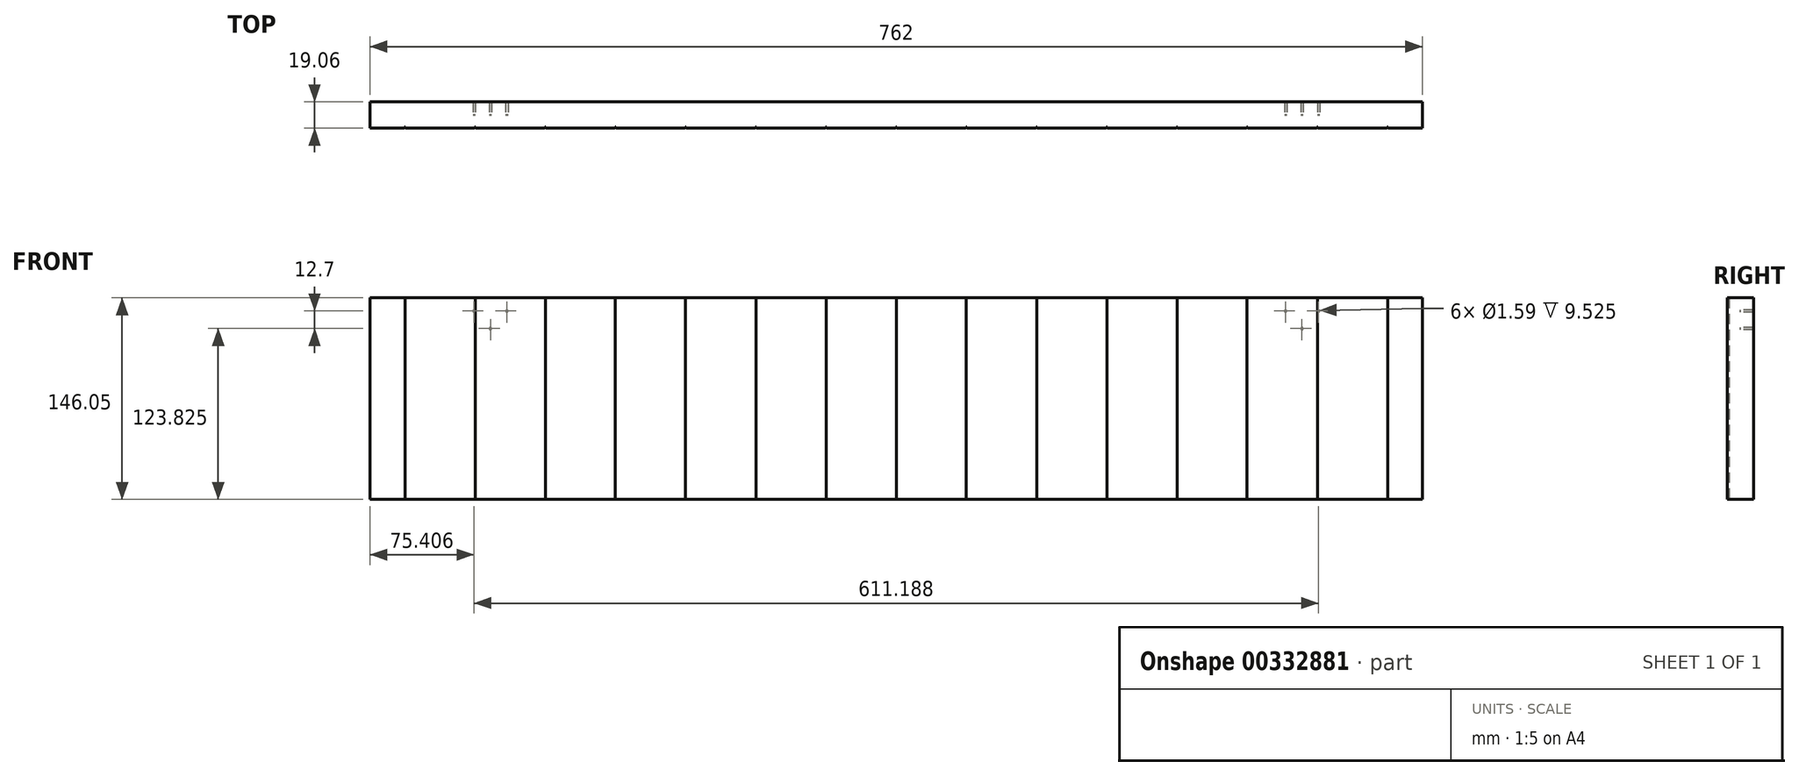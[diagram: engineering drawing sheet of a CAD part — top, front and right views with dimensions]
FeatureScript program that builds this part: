
annotation { "Feature Type Name" : "Feature", "Feature Type Description" : "" }
export const myFeature = defineFeature(function(context is Context, id is Id, definition is map)
    precondition{}
    {
        {
            var Q0;
            Q0=qCreatedBy(makeId("Top.planeOp"),FACE);
            var sketch = newSketch(context, id + "F0", { "sketchPlane" : qUnion([Q0])});
            skLineSegment(sketch, "E0.bottom", {"start": v(508, -9.53) * mm, "end": v(458.22, -9.53) * mm});
            skLineSegment(sketch, "E0.top", {"start": v(508, 9.53) * mm, "end": v(-508, 9.53) * mm});
            skLineSegment(sketch, "E0.left", {"start": v(508, 9.53) * mm, "end": v(508, -9.53) * mm});
            skLineSegment(sketch, "E0.right", {"start": v(-508, 9.53) * mm, "end": v(-508, -9.53) * mm});
            skPoint(sketch, "E0.middle", {"position": v(0, 0) * mm});
            skArc(sketch, "E1", {"start": v(-509.02, -9.53) * mm, "mid": v(-508.3, -9.23) * mm, "end": v(-508, -8.5) * mm});
            skArc(sketch, "E2", {"start": v(-508, -8.5) * mm, "mid": v(-507.7, -9.23) * mm, "end": v(-506.98, -9.52) * mm});
            skArc(sketch, "E3.1.0.0", {"start": v(-458.22, -9.53) * mm, "mid": v(-457.5, -9.23) * mm, "end": v(-457.2, -8.5) * mm});
            skArc(sketch, "E3.1.0.1", {"start": v(-457.2, -8.5) * mm, "mid": v(-456.9, -9.23) * mm, "end": v(-456.18, -9.52) * mm});
            skArc(sketch, "E3.2.0.0", {"start": v(-407.42, -9.53) * mm, "mid": v(-406.7, -9.23) * mm, "end": v(-406.4, -8.5) * mm});
            skArc(sketch, "E3.2.0.1", {"start": v(-406.4, -8.5) * mm, "mid": v(-406.1, -9.23) * mm, "end": v(-405.38, -9.52) * mm});
            skArc(sketch, "E3.3.0.0", {"start": v(-356.62, -9.53) * mm, "mid": v(-355.9, -9.23) * mm, "end": v(-355.6, -8.5) * mm});
            skArc(sketch, "E3.3.0.1", {"start": v(-355.6, -8.5) * mm, "mid": v(-355.3, -9.23) * mm, "end": v(-354.58, -9.52) * mm});
            skArc(sketch, "E3.4.0.0", {"start": v(-305.82, -9.53) * mm, "mid": v(-305.1, -9.23) * mm, "end": v(-304.8, -8.5) * mm});
            skArc(sketch, "E3.4.0.1", {"start": v(-304.8, -8.5) * mm, "mid": v(-304.5, -9.23) * mm, "end": v(-303.78, -9.52) * mm});
            skArc(sketch, "E3.5.0.0", {"start": v(-255.02, -9.53) * mm, "mid": v(-254.3, -9.23) * mm, "end": v(-254, -8.5) * mm});
            skArc(sketch, "E3.5.0.1", {"start": v(-254, -8.5) * mm, "mid": v(-253.7, -9.23) * mm, "end": v(-252.98, -9.52) * mm});
            skArc(sketch, "E3.6.0.0", {"start": v(-204.22, -9.53) * mm, "mid": v(-203.5, -9.23) * mm, "end": v(-203.2, -8.5) * mm});
            skArc(sketch, "E3.6.0.1", {"start": v(-203.2, -8.5) * mm, "mid": v(-202.9, -9.23) * mm, "end": v(-202.18, -9.52) * mm});
            skArc(sketch, "E3.7.0.0", {"start": v(-153.42, -9.53) * mm, "mid": v(-152.7, -9.23) * mm, "end": v(-152.4, -8.5) * mm});
            skArc(sketch, "E3.7.0.1", {"start": v(-152.4, -8.5) * mm, "mid": v(-152.1, -9.23) * mm, "end": v(-151.38, -9.52) * mm});
            skArc(sketch, "E3.8.0.0", {"start": v(-102.62, -9.53) * mm, "mid": v(-101.9, -9.23) * mm, "end": v(-101.6, -8.5) * mm});
            skArc(sketch, "E3.8.0.1", {"start": v(-101.6, -8.5) * mm, "mid": v(-101.3, -9.23) * mm, "end": v(-100.58, -9.52) * mm});
            skArc(sketch, "E3.9.0.0", {"start": v(-51.82, -9.53) * mm, "mid": v(-51.1, -9.23) * mm, "end": v(-50.8, -8.5) * mm});
            skArc(sketch, "E3.9.0.1", {"start": v(-50.8, -8.5) * mm, "mid": v(-50.5, -9.23) * mm, "end": v(-49.78, -9.52) * mm});
            skArc(sketch, "E3.10.0.0", {"start": v(-1.02, -9.53) * mm, "mid": v(-0.3, -9.23) * mm, "end": v(0, -8.5) * mm});
            skArc(sketch, "E3.10.0.1", {"start": v(0, -8.5) * mm, "mid": v(0.3, -9.23) * mm, "end": v(1.02, -9.52) * mm});
            skArc(sketch, "E3.11.0.0", {"start": v(49.78, -9.53) * mm, "mid": v(50.5, -9.23) * mm, "end": v(50.8, -8.5) * mm});
            skArc(sketch, "E3.11.0.1", {"start": v(50.8, -8.5) * mm, "mid": v(51.1, -9.23) * mm, "end": v(51.82, -9.52) * mm});
            skArc(sketch, "E3.12.0.0", {"start": v(100.58, -9.53) * mm, "mid": v(101.3, -9.23) * mm, "end": v(101.6, -8.5) * mm});
            skArc(sketch, "E3.12.0.1", {"start": v(101.6, -8.5) * mm, "mid": v(101.9, -9.23) * mm, "end": v(102.62, -9.52) * mm});
            skArc(sketch, "E3.13.0.0", {"start": v(151.38, -9.53) * mm, "mid": v(152.1, -9.23) * mm, "end": v(152.4, -8.5) * mm});
            skArc(sketch, "E3.13.0.1", {"start": v(152.4, -8.5) * mm, "mid": v(152.7, -9.23) * mm, "end": v(153.42, -9.52) * mm});
            skArc(sketch, "E3.14.0.0", {"start": v(202.18, -9.53) * mm, "mid": v(202.9, -9.23) * mm, "end": v(203.2, -8.5) * mm});
            skArc(sketch, "E3.14.0.1", {"start": v(203.2, -8.5) * mm, "mid": v(203.5, -9.23) * mm, "end": v(204.22, -9.52) * mm});
            skArc(sketch, "E3.15.0.0", {"start": v(252.98, -9.53) * mm, "mid": v(253.7, -9.23) * mm, "end": v(254, -8.5) * mm});
            skArc(sketch, "E3.15.0.1", {"start": v(254, -8.5) * mm, "mid": v(254.3, -9.23) * mm, "end": v(255.02, -9.52) * mm});
            skArc(sketch, "E3.16.0.0", {"start": v(303.78, -9.53) * mm, "mid": v(304.5, -9.23) * mm, "end": v(304.8, -8.5) * mm});
            skArc(sketch, "E3.16.0.1", {"start": v(304.8, -8.5) * mm, "mid": v(305.1, -9.23) * mm, "end": v(305.82, -9.52) * mm});
            skArc(sketch, "E3.17.0.0", {"start": v(354.58, -9.53) * mm, "mid": v(355.3, -9.23) * mm, "end": v(355.6, -8.5) * mm});
            skArc(sketch, "E3.17.0.1", {"start": v(355.6, -8.5) * mm, "mid": v(355.9, -9.23) * mm, "end": v(356.62, -9.52) * mm});
            skArc(sketch, "E3.18.0.0", {"start": v(405.38, -9.53) * mm, "mid": v(406.1, -9.23) * mm, "end": v(406.4, -8.5) * mm});
            skArc(sketch, "E3.18.0.1", {"start": v(406.4, -8.5) * mm, "mid": v(406.7, -9.23) * mm, "end": v(407.42, -9.52) * mm});
            skArc(sketch, "E3.19.0.0", {"start": v(456.18, -9.53) * mm, "mid": v(456.9, -9.23) * mm, "end": v(457.2, -8.5) * mm});
            skArc(sketch, "E3.19.0.1", {"start": v(457.2, -8.5) * mm, "mid": v(457.5, -9.23) * mm, "end": v(458.22, -9.52) * mm});
            skLineSegment(sketch, "E3.direction1", {"start": v(-506.98, -9.53) * mm, "end": v(-458.22, -9.53) * mm, "construction": true});
            skLineSegment(sketch, "E4.trimOffspring", {"start": v(-458.22, -9.53) * mm, "end": v(-508, -9.53) * mm});
            skLineSegment(sketch, "E5.trimOffspring", {"start": v(-407.42, -9.53) * mm, "end": v(-456.18, -9.53) * mm});
            skLineSegment(sketch, "E6.trimOffspring", {"start": v(-356.62, -9.53) * mm, "end": v(-405.38, -9.53) * mm});
            skLineSegment(sketch, "E7.trimOffspring", {"start": v(-305.82, -9.53) * mm, "end": v(-354.58, -9.53) * mm});
            skLineSegment(sketch, "E8.trimOffspring", {"start": v(-255.02, -9.53) * mm, "end": v(-303.78, -9.53) * mm});
            skLineSegment(sketch, "E9.trimOffspring", {"start": v(-204.22, -9.53) * mm, "end": v(-252.98, -9.53) * mm});
            skLineSegment(sketch, "E10.trimOffspring", {"start": v(-153.42, -9.53) * mm, "end": v(-202.18, -9.53) * mm});
            skLineSegment(sketch, "E11.trimOffspring", {"start": v(-102.62, -9.53) * mm, "end": v(-151.38, -9.53) * mm});
            skLineSegment(sketch, "E12.trimOffspring", {"start": v(-51.82, -9.53) * mm, "end": v(-100.58, -9.53) * mm});
            skLineSegment(sketch, "E13.trimOffspring", {"start": v(-1.02, -9.53) * mm, "end": v(-49.78, -9.53) * mm});
            skLineSegment(sketch, "E14.trimOffspring", {"start": v(49.78, -9.53) * mm, "end": v(1.02, -9.53) * mm});
            skLineSegment(sketch, "E15.trimOffspring", {"start": v(100.58, -9.53) * mm, "end": v(51.82, -9.53) * mm});
            skLineSegment(sketch, "E16.trimOffspring", {"start": v(151.38, -9.53) * mm, "end": v(102.62, -9.53) * mm});
            skLineSegment(sketch, "E17.trimOffspring", {"start": v(202.18, -9.53) * mm, "end": v(153.42, -9.53) * mm});
            skLineSegment(sketch, "E18.trimOffspring", {"start": v(252.98, -9.53) * mm, "end": v(204.22, -9.53) * mm});
            skLineSegment(sketch, "E19.trimOffspring", {"start": v(303.78, -9.53) * mm, "end": v(255.02, -9.53) * mm});
            skLineSegment(sketch, "E20.trimOffspring", {"start": v(354.58, -9.53) * mm, "end": v(305.82, -9.53) * mm});
            skLineSegment(sketch, "E21.trimOffspring", {"start": v(405.38, -9.53) * mm, "end": v(356.62, -9.53) * mm});
            skLineSegment(sketch, "E22.trimOffspring", {"start": v(456.18, -9.53) * mm, "end": v(407.42, -9.53) * mm});
            skSolve(sketch);
        }
        {
            var Q0;
            Q0=qSketchRegion(id+"F0",true);
            extrude(context, id + "F1", {"entities" : qUnion([Q0]), "depth" : 146.05 * mm});
        }
        {
            var Q0;
            Q0=qCreatedBy(makeId("Top.planeOp"),FACE);
            var sketch = newSketch(context, id + "F2", { "sketchPlane" : qUnion([Q0])});
            skLineSegment(sketch, "E23.bottom", {"start": v(381, -89.59) * mm, "end": v(724.07, -89.59) * mm});
            skLineSegment(sketch, "E23.top", {"start": v(381, 47.64) * mm, "end": v(724.07, 47.64) * mm});
            skLineSegment(sketch, "E23.left", {"start": v(381, -89.59) * mm, "end": v(381, 47.64) * mm});
            skLineSegment(sketch, "E23.right", {"start": v(724.07, -89.59) * mm, "end": v(724.07, 47.64) * mm});
            skLineSegment(sketch, "E24.bottom", {"start": v(-381, -137.09) * mm, "end": v(-685.36, -137.09) * mm});
            skLineSegment(sketch, "E24.top", {"start": v(-381, 58.2) * mm, "end": v(-685.36, 58.2) * mm});
            skLineSegment(sketch, "E24.left", {"start": v(-381, -137.09) * mm, "end": v(-381, 58.2) * mm});
            skLineSegment(sketch, "E24.right", {"start": v(-685.36, -137.09) * mm, "end": v(-685.36, 58.2) * mm});
            skSolve(sketch);
        }
        {
            var Q0;
            Q0=qSketchRegion(id+"F2",true);
            extrude(context, id + "F3", {"entities" : qUnion([Q0]), "operationType" : NewBodyOperationType.REMOVE, "depth" : 1143 * mm});
        }
        {
            var Q0;
            Q0=qCreatedBy(makeId("Front.planeOp"),FACE);
            var sketch = newSketch(context, id + "F4", { "sketchPlane" : qUnion([Q0])});
            skLineSegment(sketch, "E25", {"start": v(381, 136.53) * mm, "end": v(-381, 136.52) * mm, "construction": true});
            skLineSegment(sketch, "E26.bottom", {"start": v(381, 193.1) * mm, "end": v(-381, 193.1) * mm, "construction": true});
            skLineSegment(sketch, "E26.top", {"start": v(381, 79.95) * mm, "end": v(-381, 79.95) * mm, "construction": true});
            skLineSegment(sketch, "E26.left", {"start": v(381, 193.1) * mm, "end": v(381, 79.95) * mm, "construction": true});
            skLineSegment(sketch, "E26.right", {"start": v(-381, 193.1) * mm, "end": v(-381, 79.95) * mm, "construction": true});
            skPoint(sketch, "E26.middle", {"position": v(0, 136.53) * mm});
            skLineSegment(sketch, "E27", {"start": v(-293.69, 193.1) * mm, "end": v(-293.69, 79.95) * mm, "construction": true});
            skLineSegment(sketch, "E28", {"start": v(-293.69, 123.82) * mm, "end": v(293.69, 123.83) * mm, "construction": true});
            skLineSegment(sketch, "E29", {"start": v(293.69, 193.1) * mm, "end": v(293.69, 79.95) * mm, "construction": true});
            skCircle(sketch, "E30", {"center": v(-293.69, 123.82) * mm, "radius": 0.8 * mm});
            skCircle(sketch, "E31", {"center": v(-281.78, 136.52) * mm, "radius": 0.8 * mm});
            skCircle(sketch, "E32", {"center": v(-305.6, 136.52) * mm, "radius": 0.8 * mm});
            skCircle(sketch, "E33", {"center": v(293.69, 123.83) * mm, "radius": 0.8 * mm});
            skCircle(sketch, "E34", {"center": v(305.6, 136.53) * mm, "radius": 0.8 * mm});
            skCircle(sketch, "E35", {"center": v(281.78, 136.53) * mm, "radius": 0.8 * mm});
            skSolve(sketch);
        }
        {
            var Q0;
            Q0=qSketchRegion(id+"F4",true);
            extrude(context, id + "F5", {"entities" : qUnion([Q0]), "operationType" : NewBodyOperationType.REMOVE, "oppositeDirection" : true, "depth" : 25.4 * mm});
        }
    });
